# Revit family: 201_TINO-_
name_source: partatom
category: Air Terminals
units: mm (PartAtom-declared; Revit-internal decimal feet)

## family parameters
Always vertical = Yes
Cut with Voids When Loaded = No
Part Type = Normal
Room Calculation Point = Yes
Round Connector Dimension = Use Diameter
Shared = No
Work Plane-Based = No

## types (5) — shared parameters
CAT0 = Yes
CL_Location_5000 = 5000 mm  [stored 16.4042 ft]
Description = Wall diffuser
L_ARR = 400 mm  [stored 1.31234 ft]
Manufacturer = Climecon
QmdConnectorList = 201;D
URL = www.climecon.fi
W_ARR = 400 mm  [stored 1.31234 ft]
magiPartTypeId = 201
magiProductFamilyId = TINO-*
zero-valued in all types: CLBTZ, H_ARR

## per-type parameters (varying)
| type | A | AA | B1 | BB | C1 | D | R1 |
| TINO-100P | 255 mm | 128 mm | 30 mm  [stored 0.0984252 ft] | 75 mm  [stored 0.246063 ft] | 42 mm  [stored 0.137795 ft] | 100 mm | 6 mm  [stored 0.019685 ft] |
| TINO-125 | 298 mm | 149 mm | 35 mm | 88 mm | 50 mm  [stored 0.164042 ft] | 125 mm | 8 mm  [stored 0.0262467 ft] |
| TINO-125P | 298 mm | 149 mm | 35 mm | 88 mm | 50 mm  [stored 0.164042 ft] | 125 mm | 8 mm  [stored 0.0262467 ft] |
| TINO-160 | 357 mm | 179 mm | 42 mm  [stored 0.137795 ft] | 105 mm  [stored 0.344488 ft] | 62 mm | 160 mm | 9 mm  [stored 0.0295276 ft] |
| TINO-200 | 425 mm  [stored 1.39436 ft] | 213 mm | 50 mm  [stored 0.164042 ft] | 125 mm  [stored 0.410105 ft] | 77 mm | 200 mm | 11 mm |

note: column(s) folded — value = type name in every type: MC Product Code, magiProductId

note: [stored X ft] marks values corroborated as IEEE doubles in the binary element streams (Revit-internal decimal feet)

## geometry (parser evidence)
native form markers: Sweep x2
no freeform markers — native parametric forms only
